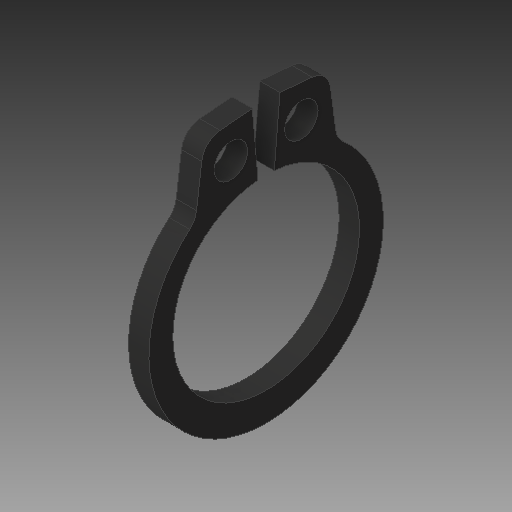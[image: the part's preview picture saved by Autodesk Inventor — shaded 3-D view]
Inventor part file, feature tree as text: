
AUTODESK INVENTOR PART (.ipt)
format: ipt  version: 2017 (Build 210142000, 142)  size: 113,152 bytes
history: native  units: in
note: dims shown in document units (in); Inventor stores cm internally (conversion verified against a paired STEP export)
features: fillet x1
ambient origin geometry x8: Origin, YZ Plane, XZ Plane, XY Plane, X Axis, Y Axis, Z Axis, Center Point
bodies: Solid1 (feature_tree)
feature tree (1):
  fillet  "Fillet1"  [1 undecoded]
note: 1 required parameter value undecoded (feature->parameter linkage not recoverable at this tier; creation-order binding heuristic only, values carry confidence <= 0.55)
